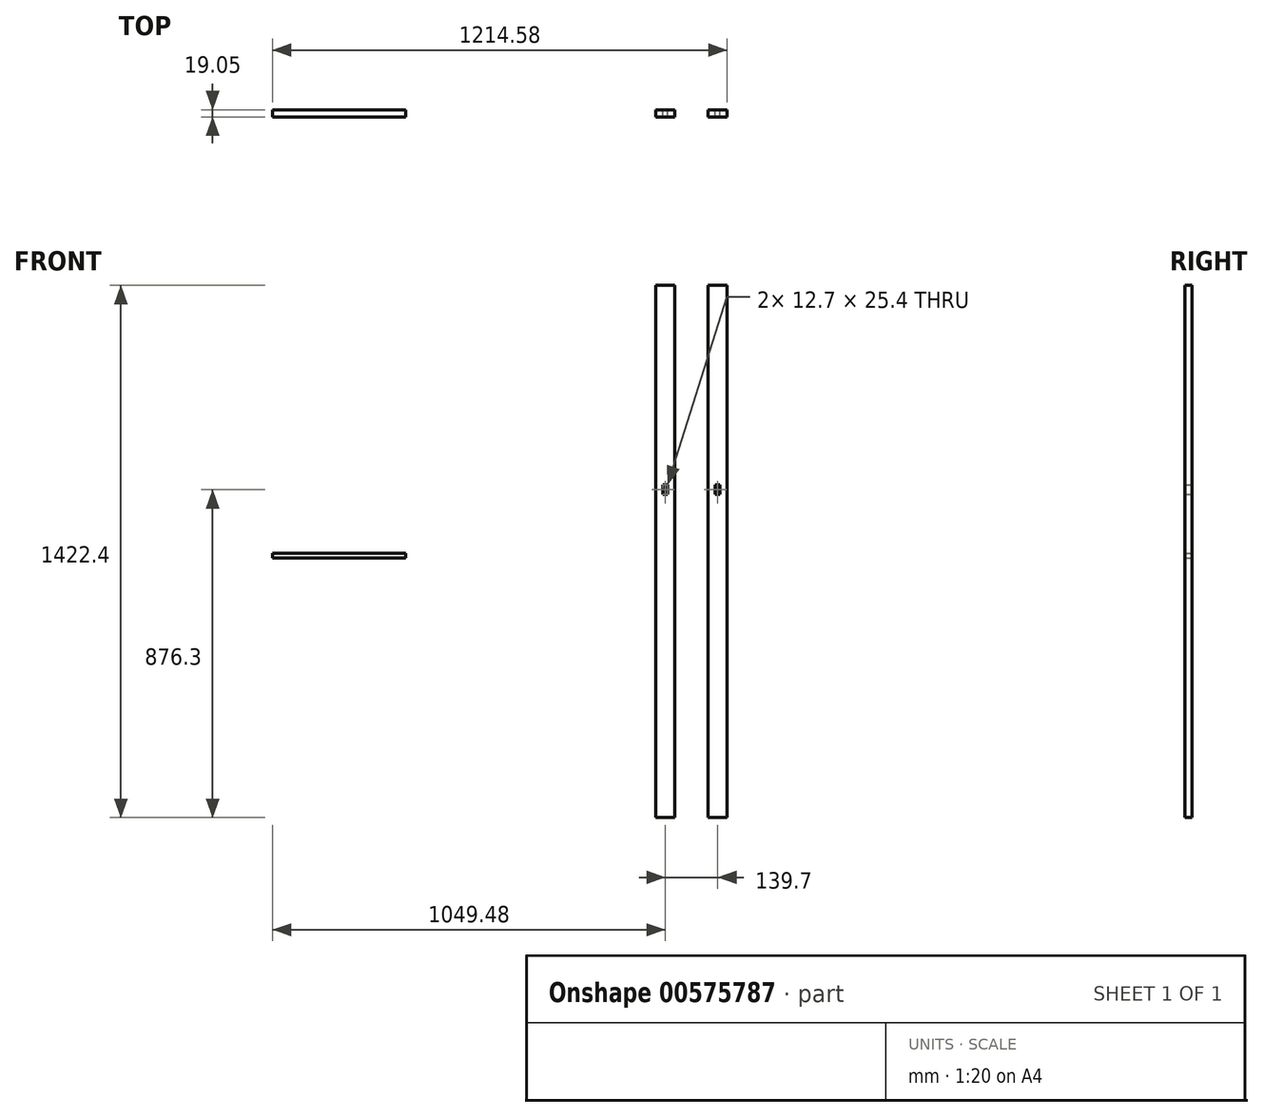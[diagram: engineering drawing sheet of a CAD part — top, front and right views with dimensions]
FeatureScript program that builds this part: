
annotation { "Feature Type Name" : "Feature", "Feature Type Description" : "" }
export const myFeature = defineFeature(function(context is Context, id is Id, definition is map)
    precondition{}
    {
        {
            var Q0;
            Q0=qCreatedBy(makeId("Front.planeOp"),FACE);
            var sketch = newSketch(context, id + "F0", { "sketchPlane" : qUnion([Q0])});
            skLineSegment(sketch, "E0", {"start": v(-82.55, 546.1) * mm, "end": v(-31.75, 546.1) * mm});
            skLineSegment(sketch, "E1", {"start": v(-31.75, 546.1) * mm, "end": v(-31.75, 12.7) * mm});
            skLineSegment(sketch, "E2", {"start": v(57.15, 12.7) * mm, "end": v(57.15, 546.1) * mm});
            skLineSegment(sketch, "E3", {"start": v(57.15, 546.1) * mm, "end": v(107.95, 546.1) * mm});
            skLineSegment(sketch, "E4", {"start": v(107.95, 546.1) * mm, "end": v(107.95, 12.7) * mm});
            skLineSegment(sketch, "E5", {"start": v(107.95, -12.7) * mm, "end": v(107.95, -876.3) * mm});
            skLineSegment(sketch, "E6", {"start": v(107.95, -876.3) * mm, "end": v(57.15, -876.3) * mm});
            skLineSegment(sketch, "E7", {"start": v(57.15, -876.3) * mm, "end": v(57.15, -12.7) * mm});
            skLineSegment(sketch, "E8", {"start": v(-31.75, -12.7) * mm, "end": v(-31.75, -876.3) * mm});
            skLineSegment(sketch, "E9", {"start": v(-31.75, -876.3) * mm, "end": v(-82.55, -876.3) * mm});
            skLineSegment(sketch, "E10", {"start": v(-82.55, -876.3) * mm, "end": v(-82.55, -12.7) * mm});
            skLineSegment(sketch, "E11", {"start": v(-82.55, 12.7) * mm, "end": v(-82.55, 546.1) * mm});
            skPoint(sketch, "E12", {"position": v(0, 0) * mm});
            skLineSegment(sketch, "E13", {"start": v(107.95, 12.7) * mm, "end": v(107.95, -12.7) * mm});
            skLineSegment(sketch, "E14", {"start": v(57.15, 12.7) * mm, "end": v(57.15, -12.7) * mm});
            skLineSegment(sketch, "E15", {"start": v(-82.55, 12.7) * mm, "end": v(-82.55, -12.7) * mm});
            skLineSegment(sketch, "E16", {"start": v(-31.75, 12.7) * mm, "end": v(-31.75, -12.7) * mm});
            skLineSegment(sketch, "E17", {"start": v(-751.03, -170.42) * mm, "end": v(-1106.63, -170.42) * mm});
            skLineSegment(sketch, "E18", {"start": v(-1106.63, -170.42) * mm, "end": v(-1106.63, -183.12) * mm});
            skLineSegment(sketch, "E19", {"start": v(-1106.63, -183.12) * mm, "end": v(-751.03, -183.12) * mm});
            skLineSegment(sketch, "E20", {"start": v(-751.03, -183.12) * mm, "end": v(-751.03, -170.42) * mm});
            skLineSegment(sketch, "E21", {"start": v(-63.5, 12.7) * mm, "end": v(-50.8, 12.7) * mm});
            skLineSegment(sketch, "E22", {"start": v(-50.8, 12.7) * mm, "end": v(-50.8, -12.7) * mm});
            skLineSegment(sketch, "E23", {"start": v(-50.8, -12.7) * mm, "end": v(-63.5, -12.7) * mm});
            skLineSegment(sketch, "E24", {"start": v(-63.5, -12.7) * mm, "end": v(-63.5, 12.7) * mm});
            skLineSegment(sketch, "E25", {"start": v(76.2, 12.7) * mm, "end": v(88.9, 12.7) * mm});
            skLineSegment(sketch, "E26", {"start": v(88.9, 12.7) * mm, "end": v(88.9, -12.7) * mm});
            skLineSegment(sketch, "E27", {"start": v(88.9, -12.7) * mm, "end": v(76.2, -12.7) * mm});
            skLineSegment(sketch, "E28", {"start": v(76.2, -12.7) * mm, "end": v(76.2, 12.7) * mm});
            skSolve(sketch);
        }
        {
            var Q0;
            Q0=makeQuery(id+"F0.imprint","IMPRINT",FACE,{"disambiguationData":[TD([[makeQuery(id+"F0.imprint","IMPRINT",EDGE,{"derivedFrom":sQuery(id+"F0.wireOp",EDGE,"E2")}),-1.0]])]});
            var Q1;
            Q1=makeQuery(id+"F0.imprint","IMPRINT",FACE,{"disambiguationData":[TD([[makeQuery(id+"F0.imprint","IMPRINT",EDGE,{"derivedFrom":sQuery(id+"F0.wireOp",EDGE,"E0")}),-1.0]])]});
            var Q2;
            Q2=makeQuery(id+"F0.imprint","IMPRINT",FACE,{"disambiguationData":[TD([[makeQuery(id+"F0.imprint","IMPRINT",EDGE,{"derivedFrom":sQuery(id+"F0.wireOp",EDGE,"E17")}),1.0]])]});
            extrude(context, id + "F1", {"entities" : qUnion([Q0, Q1, Q2]), "depth" : 19.05 * mm, "offsetDistance" : 25.4 * mm});
        }
    });
